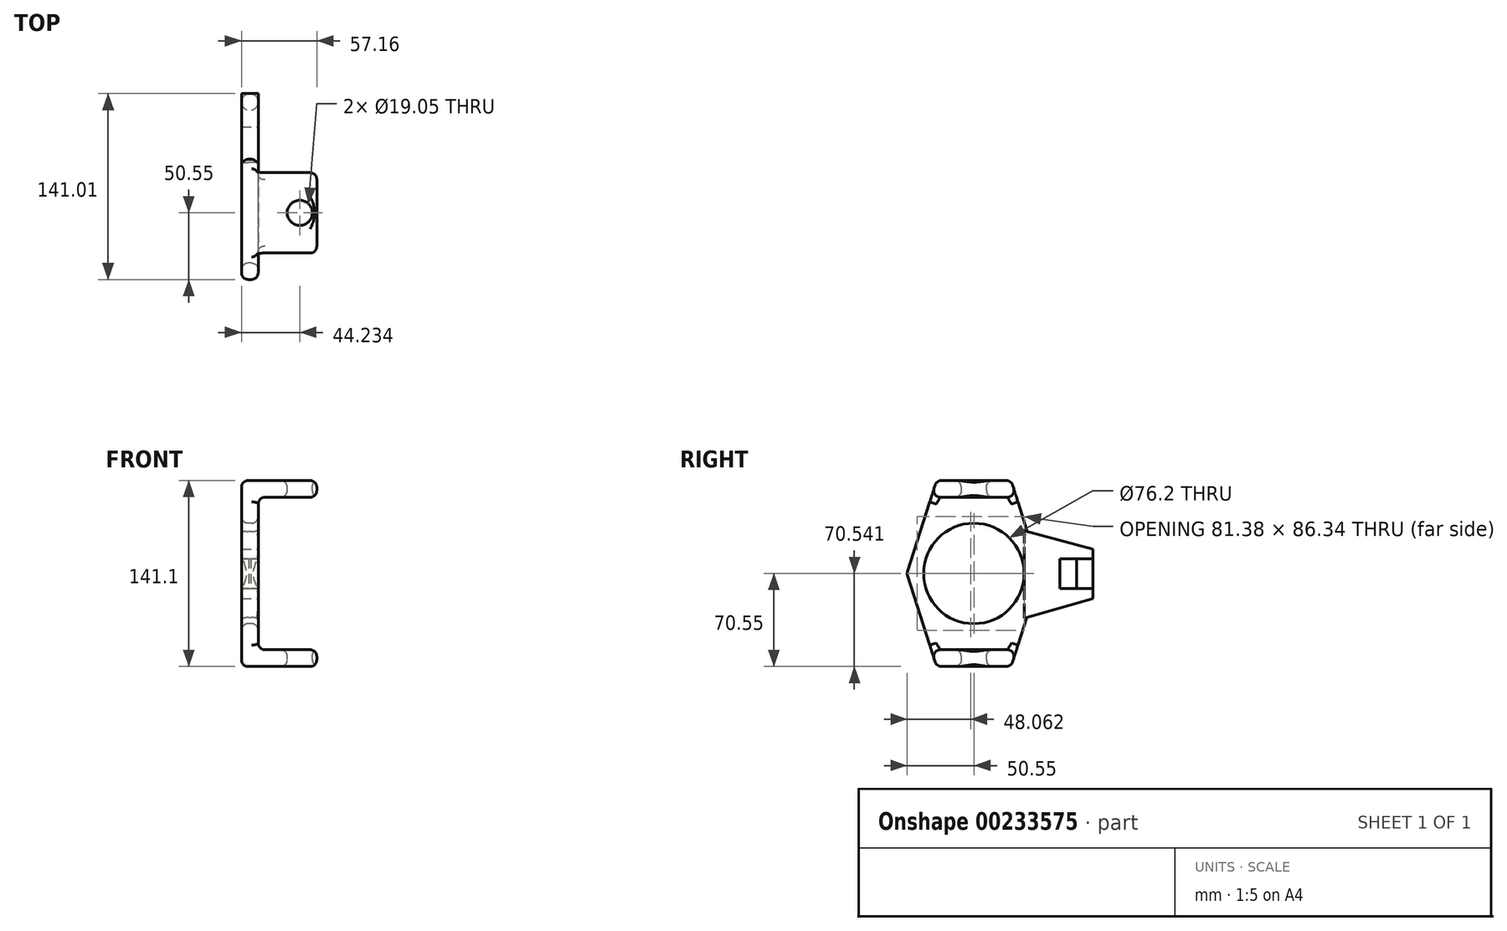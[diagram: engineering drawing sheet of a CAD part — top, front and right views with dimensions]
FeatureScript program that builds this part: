
annotation { "Feature Type Name" : "Feature", "Feature Type Description" : "" }
export const myFeature = defineFeature(function(context is Context, id is Id, definition is map)
    precondition{}
    {
        {
            var Q0;
            Q0=qCreatedBy(makeId("Front.planeOp"),FACE);
            var sketch = newSketch(context, id + "F0", { "sketchPlane" : qUnion([Q0])});
            skLineSegment(sketch, "E0.bottom", {"start": v(22.22, 57.85) * mm, "end": v(-22.23, 57.85) * mm});
            skLineSegment(sketch, "E0.top", {"start": v(22.22, -57.85) * mm, "end": v(-22.23, -57.85) * mm});
            skLineSegment(sketch, "E0.right", {"start": v(-22.23, 57.85) * mm, "end": v(-22.23, -57.85) * mm});
            skPoint(sketch, "E0.middle", {"position": v(0, 0) * mm});
            skLineSegment(sketch, "E1.0", {"start": v(22.22, -70.55) * mm, "end": v(-34.93, -70.55) * mm});
            skLineSegment(sketch, "E1.1", {"start": v(-34.93, 70.55) * mm, "end": v(-34.93, -70.55) * mm});
            skLineSegment(sketch, "E1.2", {"start": v(22.22, 70.55) * mm, "end": v(-34.93, 70.55) * mm});
            skLineSegment(sketch, "E2", {"start": v(22.22, 70.55) * mm, "end": v(22.22, 57.85) * mm});
            skLineSegment(sketch, "E3", {"start": v(22.22, -57.85) * mm, "end": v(22.22, -70.55) * mm});
            skSolve(sketch);
        }
        {
            var Q0;
            Q0=makeQuery(id+"F0.imprint","IMPRINT",FACE,{"disambiguationData":[TD([[makeQuery(id+"F0.imprint","IMPRINT",EDGE,{"derivedFrom":sQuery(id+"F0.wireOp",EDGE,"E0.bottom")}),-1.0]])]});
            extrude(context, id + "F1", {"entities" : qUnion([Q0]), "depth" : 101.6 * mm});
        }
        {
            var Q0;
            Q0=makeQuery(id+"F1.opExtrude","SWEPT_FACE",FACE,{"disambiguationData":[OSD([sQuery(id+"F0.wireOp",EDGE,"E1.1")])]});
            var sketch = newSketch(context, id + "F2", { "sketchPlane" : qUnion([Q0])});
            skCircle(sketch, "E4", {"center": v(50.8, 0) * mm, "radius": 38.1 * mm});
            skPoint(sketch, "E4.centerSnap0", {"position": v(50.8, -70.55) * mm});
            skLineSegment(sketch, "E5.bottom", {"start": v(79.08, -70.55) * mm, "end": v(22.52, -70.55) * mm, "construction": true});
            skLineSegment(sketch, "E5.top", {"start": v(79.08, 70.55) * mm, "end": v(22.52, 70.55) * mm, "construction": true});
            skLineSegment(sketch, "E5.left", {"start": v(79.08, -70.55) * mm, "end": v(79.08, 70.55) * mm, "construction": true});
            skLineSegment(sketch, "E5.right", {"start": v(22.52, -70.55) * mm, "end": v(22.52, 70.55) * mm, "construction": true});
            skLineSegment(sketch, "E6", {"start": v(79.08, -70.55) * mm, "end": v(101.6, 0) * mm});
            skLineSegment(sketch, "E7", {"start": v(101.6, 0) * mm, "end": v(79.08, 70.55) * mm});
            skLineSegment(sketch, "E8", {"start": v(22.52, 70.55) * mm, "end": v(0, 0) * mm});
            skLineSegment(sketch, "E9", {"start": v(0, 0) * mm, "end": v(22.52, -70.55) * mm});
            skSolve(sketch);
        }
        {
            var Q0;
            {var subQ0=sQuery(id+"F2.wireOp",EDGE,"E9");Q0=makeQuery(id+"F2.imprint","IMPRINT",FACE,{"disambiguationData":[TD([[makeQuery(id+"F2.imprint","IMPRINT",EDGE,{"derivedFrom":subQ0}),-1.0]])]});}
            var Q1;
            {var subQ0=sQuery(id+"F2.wireOp",EDGE,"E8");Q1=makeQuery(id+"F2.imprint","IMPRINT",FACE,{"disambiguationData":[TD([[makeQuery(id+"F2.imprint","IMPRINT",EDGE,{"derivedFrom":subQ0}),-1.0]])]});}
            var Q2;
            {var subQ0=sQuery(id+"F2.wireOp",EDGE,"E7");Q2=makeQuery(id+"F2.imprint","IMPRINT",FACE,{"disambiguationData":[TD([[makeQuery(id+"F2.imprint","IMPRINT",EDGE,{"derivedFrom":subQ0}),-1.0]])]});}
            var Q3;
            {var subQ0=sQuery(id+"F2.wireOp",EDGE,"E6");Q3=makeQuery(id+"F2.imprint","IMPRINT",FACE,{"disambiguationData":[TD([[makeQuery(id+"F2.imprint","IMPRINT",EDGE,{"derivedFrom":subQ0}),-1.0]])]});}
            var Q4;
            Q4=makeQuery(id+"F2.imprint","IMPRINT",FACE,{"disambiguationData":[TD([[makeQuery(id+"F2.imprint","IMPRINT",EDGE,{"derivedFrom":sQuery(id+"F2.wireOp",EDGE,"E4")}),1.0]])]});
            extrude(context, id + "F3", {"entities" : qUnion([Q0, Q1, Q2, Q3, Q4]), "operationType" : NewBodyOperationType.REMOVE, "endBound" : BoundingType.THROUGH_ALL, "oppositeDirection" : true, "depth" : 25.4 * mm});
        }
        {
            var Q0;
            Q0=makeQuery(id+"F1.opExtrude","SWEPT_FACE",FACE,{"disambiguationData":[OSD([sQuery(id+"F0.wireOp",EDGE,"E1.2")])]});
            var sketch = newSketch(context, id + "F4", { "sketchPlane" : qUnion([Q0])});
            skCircle(sketch, "E10", {"center": v(9.3, -50.8) * mm, "radius": 9.53 * mm});
            skPoint(sketch, "E10.centerSnap0", {"position": v(22.22, -50.8) * mm});
            skSolve(sketch);
        }
        {
            var Q0;
            Q0=makeQuery(id+"F4.imprint","IMPRINT",FACE,{"disambiguationData":[TD([[makeQuery(id+"F4.imprint","IMPRINT",EDGE,{"derivedFrom":sQuery(id+"F4.wireOp",EDGE,"E10")}),1.0]])]});
            extrude(context, id + "F5", {"entities" : qUnion([Q0]), "operationType" : NewBodyOperationType.REMOVE, "endBound" : BoundingType.THROUGH_ALL, "oppositeDirection" : true, "depth" : 25.4 * mm});
        }
        {
            var Q0;
            Q0=makeQuery(id+"F3.boolean.opBoolean","COPY",EDGE,{"derivedFrom":makeQuery(id+"F3.opExtrude","SWEPT_EDGE",EDGE,{"disambiguationData":[OSD([sQuery(id+"F0.wireOp",EDGE,"E1.1"),sQuery(id+"F0.wireOp",EDGE,"E1.2"),sQuery(id+"F2.wireOp",EDGE,"E8")])]})});
            var Q1;
            Q1=makeQuery(id+"F1.opExtrude","SWEPT_EDGE",EDGE,{"disambiguationData":[OSD([sQuery(id+"F0.wireOp",EDGE,"E1.1"),sQuery(id+"F0.wireOp",EDGE,"E1.2")])]});
            var Q2;
            Q2=makeQuery(id+"F3.boolean.opBoolean","COPY",EDGE,{"derivedFrom":makeQuery(id+"F3.opExtrude","SWEPT_EDGE",EDGE,{"disambiguationData":[OSD([sQuery(id+"F0.wireOp",EDGE,"E1.1"),sQuery(id+"F0.wireOp",EDGE,"E1.2"),sQuery(id+"F2.wireOp",EDGE,"E7")])]})});
            var Q3;
            Q3=makeQuery(id+"F1.opExtrude","SWEPT_EDGE",EDGE,{"disambiguationData":[OSD([sQuery(id+"F0.wireOp",EDGE,"E1.2"),sQuery(id+"F0.wireOp",EDGE,"E2")])]});
            var Q4;
            Q4=makeQuery(id+"F1.opExtrude","SWEPT_FACE",FACE,{"disambiguationData":[OSD([sQuery(id+"F0.wireOp",EDGE,"E1.1")])]});
            var Q5;
            Q5=makeQuery(id+"F3.boolean.opBoolean","COPY",FACE,{"derivedFrom":makeQuery(id+"F3.opExtrude","SWEPT_FACE",FACE,{"disambiguationData":[OSD([sQuery(id+"F2.wireOp",EDGE,"E8")])]})});
            var Q6;
            Q6=makeQuery(id+"F3.boolean.opBoolean","COPY",FACE,{"derivedFrom":makeQuery(id+"F3.opExtrude","SWEPT_FACE",FACE,{"disambiguationData":[OSD([sQuery(id+"F2.wireOp",EDGE,"E9")])]})});
            var Q7;
            Q7=makeQuery(id+"F1.opExtrude","SWEPT_FACE",FACE,{"disambiguationData":[OSD([sQuery(id+"F0.wireOp",EDGE,"E1.0")])]});
            var Q8;
            Q8=makeQuery(id+"F3.boolean.opBoolean","COPY",FACE,{"derivedFrom":makeQuery(id+"F3.opExtrude","SWEPT_FACE",FACE,{"disambiguationData":[OSD([sQuery(id+"F2.wireOp",EDGE,"E6")])]})});
            var Q9;
            Q9=makeQuery(id+"F3.boolean.opBoolean","COPY",FACE,{"derivedFrom":makeQuery(id+"F3.opExtrude","SWEPT_FACE",FACE,{"disambiguationData":[OSD([sQuery(id+"F2.wireOp",EDGE,"E7")])]})});
            var Q10;
            Q10=makeQuery(id+"F1.opExtrude","SWEPT_FACE",FACE,{"disambiguationData":[OSD([sQuery(id+"F0.wireOp",EDGE,"E0.bottom")])]});
            var Q11;
            Q11=makeQuery(id+"F1.opExtrude","SWEPT_FACE",FACE,{"disambiguationData":[OSD([sQuery(id+"F0.wireOp",EDGE,"E0.top")])]});
            var Q12;
            Q12=makeQuery(id+"F1.opExtrude","SWEPT_FACE",FACE,{"disambiguationData":[OSD([sQuery(id+"F0.wireOp",EDGE,"E1.2")])]});
            var Q13;
            Q13=makeQuery(id+"F3.boolean.opBoolean","INTERSECT",EDGE,{"derivedFrom":[makeQuery(id+"F1.opExtrude","SWEPT_FACE",FACE,{"disambiguationData":[OSD([sQuery(id+"F0.wireOp",EDGE,"E0.right")])]}),makeQuery(id+"F3.opExtrude","SWEPT_FACE",FACE,{"disambiguationData":[OSD([sQuery(id+"F2.wireOp",EDGE,"E4")])]})]});
            fillet(context, id + "F6", {"entities" : qUnion([Q0, Q1, Q2, Q3, Q4, Q5, Q6, Q7, Q8, Q9, Q10, Q11, Q12, Q13]), "radius" : 5.08 * mm, "tangentPropagation" : true, "allowEdgeOverflow" : false});
        }
        {
            var Q0;
            Q0=qCreatedBy(makeId("Right.planeOp"),FACE);
            var sketch = newSketch(context, id + "F7", { "sketchPlane" : qUnion([Q0])});
            skLineSegment(sketch, "E11.left", {"start": v(-12.6, 32.52) * mm, "end": v(-12.6, -33.96) * mm});
            skLineSegment(sketch, "E12.right", {"start": v(-12.6, -11.3) * mm, "end": v(-12.6, 11.3) * mm, "construction": true});
            skPoint(sketch, "E12.middle", {"position": v(27.22, 0) * mm});
            skPoint(sketch, "E12.middle.positionSnap0", {"position": v(27.22, 32.52) * mm});
            skPoint(sketch, "E12.centerSnap0", {"position": v(27.22, 32.52) * mm});
            skLineSegment(sketch, "E13", {"start": v(-12.6, 32.52) * mm, "end": v(39.66, 18.6) * mm});
            skLineSegment(sketch, "E14", {"start": v(39.66, -19.09) * mm, "end": v(-12.6, -33.96) * mm});
            skLineSegment(sketch, "E15", {"start": v(39.66, 18.6) * mm, "end": v(39.66, 11.3) * mm});
            skLineSegment(sketch, "E16.trimOffspring", {"start": v(39.66, -11.3) * mm, "end": v(39.66, -19.09) * mm});
            skLineSegment(sketch, "E17", {"start": v(39.66, -19.09) * mm, "end": v(39.66, -11.3) * mm});
            skLineSegment(sketch, "E18.bottom", {"start": v(39.66, -11.3) * mm, "end": v(14.3, -11.3) * mm});
            skLineSegment(sketch, "E18.top", {"start": v(39.66, 11.3) * mm, "end": v(14.3, 11.3) * mm});
            skLineSegment(sketch, "E18.right", {"start": v(14.3, -11.3) * mm, "end": v(14.3, 11.3) * mm});
            skPoint(sketch, "E19.orphan", {"position": v(39.66, -33.96) * mm});
            skPoint(sketch, "E20.start.orphan", {"position": v(67.05, -11.3) * mm});
            skPoint(sketch, "E11.right.end.orphan", {"position": v(67.05, 11.3) * mm});
            skPoint(sketch, "E11.bottom.end.orphan", {"position": v(67.05, 32.52) * mm});
            skLineSegment(sketch, "E21.trimOffspring", {"start": v(39.66, 11.3) * mm, "end": v(39.66, 18.6) * mm});
            skSolve(sketch);
        }
        {
            var Q0;
            Q0=makeQuery(id+"F7.imprint","IMPRINT",FACE,{"disambiguationData":[TD([[makeQuery(id+"F7.imprint","IMPRINT",EDGE,{"derivedFrom":sQuery(id+"F7.wireOp",EDGE,"E11.left")}),1.0]])]});
            var Q1;
            Q1=makeQuery(id+"F1.opExtrude","SWEPT_FACE",FACE,{"disambiguationData":[OSD([sQuery(id+"F0.wireOp",EDGE,"E0.right")])]});
            extrude(context, id + "F8", {"entities" : qUnion([Q0]), "operationType" : NewBodyOperationType.ADD, "oppositeDirection" : true, "depth" : 34.92 * mm, "hasSecondDirection" : true, "secondDirectionBound" : SecondDirectionBoundingType.UP_TO_SURFACE, "secondDirectionOppositeDirection" : true, "secondDirectionBoundEntityFace" : qUnion([Q1]), "secondDirectionDepth" : 25.4 * mm});
        }
        {
            var Q0;
            Q0=makeQuery(id+"F8.opExtrude","SWEPT_FACE",FACE,{"disambiguationData":[OSD([sQuery(id+"F7.wireOp",EDGE,"E18.bottom")])]});
            var sketch = newSketch(context, id + "F9", { "sketchPlane" : qUnion([Q0])});
            skCircle(sketch, "E22", {"center": v(-28.58, 33.36) * mm, "radius": 6.35 * mm});
            skPoint(sketch, "E22.centerSnap0", {"position": v(-28.58, 39.66) * mm});
            skSolve(sketch);
        }
        {
            var Q0;
            {var subQ0=sQuery(id+"F9.wireOp",EDGE,"E22");var subQ1=sQuery(id+"F7.wireOp",EDGE,"E18.bottom");var subQ4=makeQuery(id+"F9.imprint","INTERSECT",VERTEX,{"derivedFrom":[makeQuery(id+"F8.opExtrude","CAP_EDGE",EDGE,{"disambiguationData":[OSD([subQ1])],"isStart":true}),subQ0]});Q0=makeQuery(id+"F9.imprint","IMPRINT",FACE,{"disambiguationData":[TD([[makeQuery(id+"F9.imprint","IMPRINT",EDGE,{"disambiguationData":[TD([[subQ4,1.0]])],"derivedFrom":subQ0}),1.0]])]});}
            var Q1;
            Q1=makeQuery(id+"F8.opExtrude","SWEPT_FACE",FACE,{"disambiguationData":[OSD([sQuery(id+"F7.wireOp",EDGE,"E18.top")])]});
            extrude(context, id + "F10", {"entities" : qUnion([Q0]), "operationType" : NewBodyOperationType.ADD, "endBound" : BoundingType.UP_TO_SURFACE, "endBoundEntityFace" : qUnion([Q1]), "depth" : 25.4 * mm});
        }
    });
